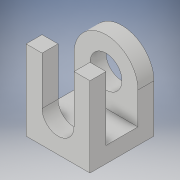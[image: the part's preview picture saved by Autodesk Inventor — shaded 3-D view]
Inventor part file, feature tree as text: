
AUTODESK INVENTOR PART (.ipt)
format: ipt  version: 2018 (Build 220112000, 112)  size: 134,656 bytes
history: native  units: mm
features: extrude x3, sketch x3
ambient origin geometry x8: Origin, YZ Plane, XZ Plane, XY Plane, X Axis, Y Axis, Z Axis, Center Point
bodies: Solid1 (feature_tree)
feature tree (6):
  extrude  "Extrusion1"  Depth=25.0mm
  extrude  "Extrusion2"  Depth=20.0mm
  extrude  "Extrusion3"  Depth=5.0mm
  sketch  "Sketch1"  dims[d0=20.0mm d1=25.0mm]
  sketch  "Sketch2"  dims[d2=5.0mm d3=20.0mm]
  sketch  "Sketch3"  dims[d4=10.0mm d5=5.0mm d6=5.0mm d7=0.0mm d8=5.0mm d9=15.0mm d10=0.0mm d11=10.0mm d12=10.0mm d13=5.0mm d14=0.0mm]
